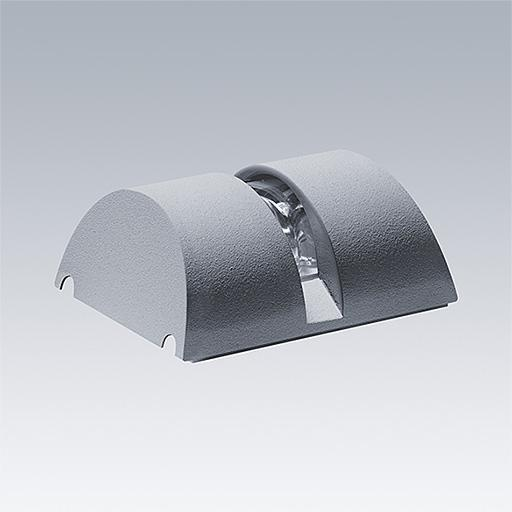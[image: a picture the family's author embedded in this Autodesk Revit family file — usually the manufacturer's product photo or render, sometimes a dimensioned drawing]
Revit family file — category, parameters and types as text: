
# Revit family: Thorn AXYL ETCH S
name_source: partatom
category: Lighting Fixtures
units: mm (PartAtom-declared; Revit-internal decimal feet)

## family parameters
Cut with Voids When Loaded = Yes
Host = Face
Light Source = Yes
Maintain Annotation Orientation = No
Part Type = Normal
Room Calculation Point = Yes
Round Connector Dimension = Use Diameter
Shared = No

## types (4) — shared parameters
Apparent Load = 11 VA
Assembly Code = Pr_70_70_48_93
Color Filter = 16777215
Default Elevation = 1000 mm  [stored 3.28084 ft]
Description = Wall Mounted Luminaire
Dimming Lamp Color Temperature Shift = <None>
Export Type to IFC As = IfcLightFixtureType
Lamp = LED
Luminaire Height = 130 mm  [stored 0.426509 ft]
Luminaire Length = 55 mm  [stored 0.180446 ft]
Luminaire Width = 105 mm  [stored 0.344488 ft]
Manufacturer = Thorn Lighting
Power Factor = 0.6
Tilt Angle = 90.00°
Type IFC Predefined Type = DIRECTIONSOURCE
URL = https://www.thornlighting.com

## per-type parameters (varying)
| type | Material Housing | Model | Photometric Web File | Type Image |
| AXYL ETCH S WF 1L RGBW EB DMX ANT | Thorn-Aluminium-RAL 7016-Anthracite Grey | 96801485 | 96801485_(STD).IES | TLG_AXYL_F_ETCH_F_S_RGBW_ANT.jpg |
| AXYL ETCH S WF 1L RGBW EB DMX BK | Thorn-Aluminium-RAL 9005-Jet Black | 96801483 | 96801483_(STD).IES | TLG_AXYL_F_ETCH_F_S_RGBW_BK.jpg |
| AXYL ETCH S WF 1L RGBW EB DMX GY | Thorn-Aluminium-RAL 9006-White Aluminium | 96801484 | 96801484_(STD).IES | TLG_AXYL_F_ETCH_F_S_RGBW_GY.jpg |
| AXYL ETCH S WF 1L RGBW EB DMX WH | Thorn-Aluminium-RAL 9016-Traffic White | 96801482 | 96801482_(STD).IES | TLG_AXYL_F_ETCH_F_S_RGBW_WH.jpg |

note: [stored X ft] marks values corroborated as IEEE doubles in the binary element streams (Revit-internal decimal feet)

## geometry (parser evidence)
native form markers: Sweep x4
no freeform markers — native parametric forms only
